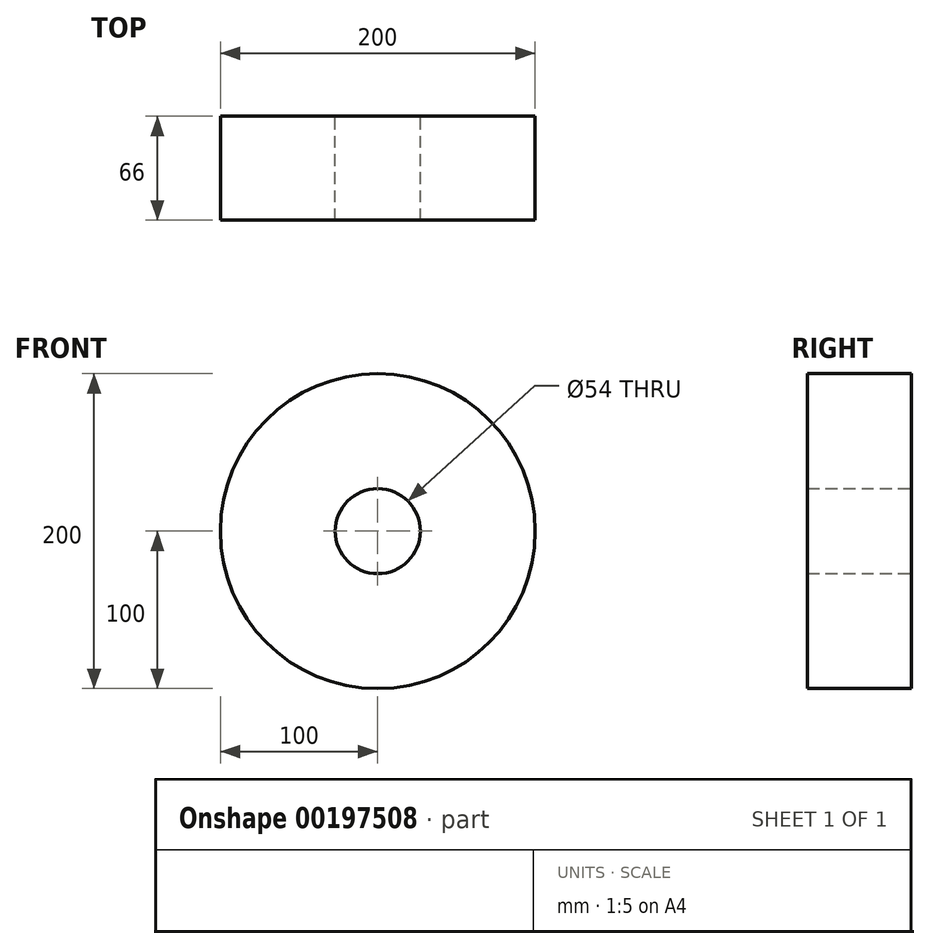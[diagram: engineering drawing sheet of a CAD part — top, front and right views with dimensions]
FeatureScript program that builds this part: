
annotation { "Feature Type Name" : "Feature", "Feature Type Description" : "" }
export const myFeature = defineFeature(function(context is Context, id is Id, definition is map)
    precondition{}
    {
        {
            var Q0;
            Q0=qCreatedBy(makeId("Front.planeOp"),FACE);
            var sketch = newSketch(context, id + "F0", { "sketchPlane" : qUnion([Q0])});
            skCircle(sketch, "E0", {"center": v(0, 0) * mm, "radius": 27 * mm});
            skCircle(sketch, "E1", {"center": v(0, 0) * mm, "radius": 100 * mm});
            skSolve(sketch);
        }
        {
            var Q0;
            Q0=qSketchRegion(id+"F0",true);
            extrude(context, id + "F1", {"entities" : qUnion([Q0]), "depth" : 66 * mm});
        }
    });
